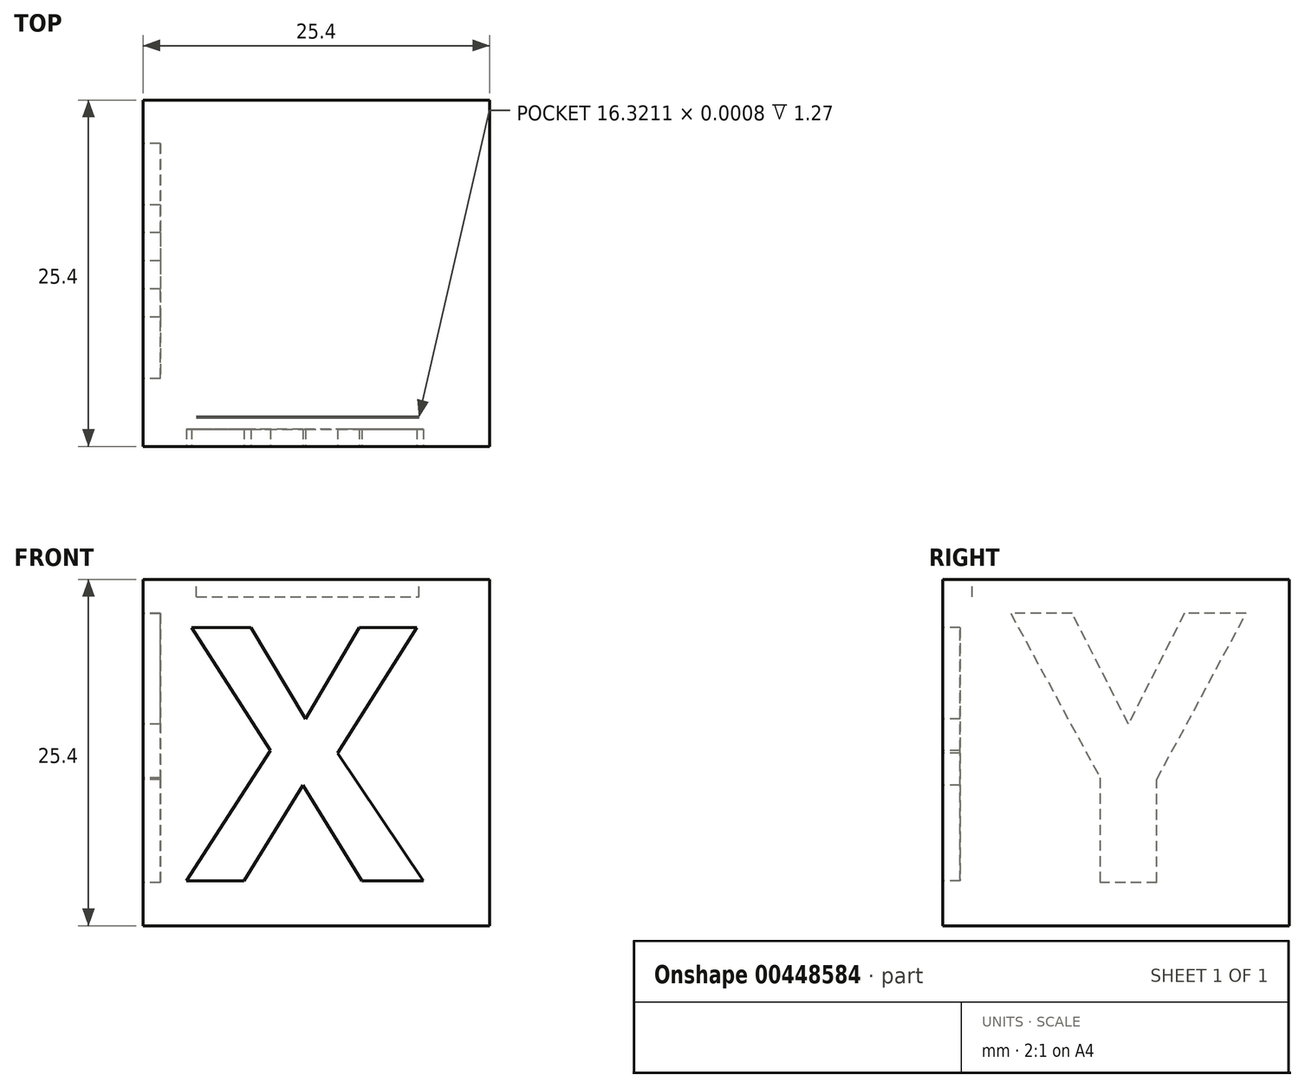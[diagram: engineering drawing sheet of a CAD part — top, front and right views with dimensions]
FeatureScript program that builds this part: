
annotation { "Feature Type Name" : "Feature", "Feature Type Description" : "" }
export const myFeature = defineFeature(function(context is Context, id is Id, definition is map)
    precondition{}
    {
        {
            var Q0;
            Q0=qCreatedBy(makeId("Top.planeOp"),FACE);
            var sketch = newSketch(context, id + "F0", { "sketchPlane" : qUnion([Q0])});
            skLineSegment(sketch, "E0.bottom", {"start": v(12.7, 12.7) * mm, "end": v(-12.7, 12.7) * mm});
            skLineSegment(sketch, "E0.top", {"start": v(12.7, -12.7) * mm, "end": v(-12.7, -12.7) * mm});
            skLineSegment(sketch, "E0.left", {"start": v(12.7, 12.7) * mm, "end": v(12.7, -12.7) * mm});
            skLineSegment(sketch, "E0.right", {"start": v(-12.7, 12.7) * mm, "end": v(-12.7, -12.7) * mm});
            skPoint(sketch, "E0.middle", {"position": v(0, 0) * mm});
            skSolve(sketch);
        }
        {
            var Q0;
            Q0=makeQuery(id+"F0.imprint","IMPRINT",FACE,{"disambiguationData":[TD([[makeQuery(id+"F0.imprint","IMPRINT",EDGE,{"derivedFrom":sQuery(id+"F0.wireOp",EDGE,"E0.bottom")}),1.0]])]});
            extrude(context, id + "F1", {"entities" : qUnion([Q0]), "depth" : 25.4 * mm, "offsetDistance" : 25.4 * mm});
        }
        {
            var Q0;
            Q0=makeQuery(id+"F1.opExtrude","SWEPT_FACE",FACE,{"disambiguationData":[OSD([sQuery(id+"F0.wireOp",EDGE,"E0.top")])]});
            var sketch = newSketch(context, id + "F2", { "sketchPlane" : qUnion([Q0])});
            skLineSegment(sketch, "E1.bottom", {"start": v(9.53, 3.28) * mm, "end": v(-9.53, 3.28) * mm, "construction": true});
            skLineSegment(sketch, "E1.top", {"start": v(9.53, 22.02) * mm, "end": v(-9.53, 22.02) * mm, "construction": true});
            skLineSegment(sketch, "E1.left", {"start": v(9.53, 3.28) * mm, "end": v(9.53, 22.02) * mm, "construction": true});
            skLineSegment(sketch, "E1.right", {"start": v(-9.53, 3.28) * mm, "end": v(-9.53, 22.02) * mm, "construction": true});
            skPoint(sketch, "E1.middle", {"position": v(0, 12.65) * mm});
            skText(sketch, "E2", { "text": "X", "fontName": "OpenSans-Bold.ttf"});
            const initialGuessF2  = {"E2": [-0.00953, 0.00328, 1, 0, 0.01874]};
            skSetInitialGuess(sketch, initialGuessF2);
            skSolve(sketch);
        }
        {
            var Q0;
            Q0=makeQuery(id+"F2.imprint","IMPRINT",FACE,{"disambiguationData":[TD([[makeQuery(id+"F2.imprint","IMPRINT",EDGE,{"derivedFrom":sQuery(id+"F2.wireOp",EDGE,"E2.sketch_text.stroke-0")}),-1.0]])]});
            extrude(context, id + "F3", {"entities" : qUnion([Q0]), "operationType" : NewBodyOperationType.REMOVE, "oppositeDirection" : true, "depth" : 1.27 * mm, "offsetDistance" : 25.4 * mm});
        }
        {
            var Q0;
            Q0=makeQuery(id+"F1.opExtrude","SWEPT_FACE",FACE,{"disambiguationData":[OSD([sQuery(id+"F0.wireOp",EDGE,"E0.right")])]});
            var sketch = newSketch(context, id + "F4", { "sketchPlane" : qUnion([Q0])});
            skLineSegment(sketch, "E3.bottom", {"start": v(-9.53, 3.18) * mm, "end": v(9.53, 3.18) * mm});
            skLineSegment(sketch, "E3.top", {"start": v(-9.53, 23.08) * mm, "end": v(9.52, 23.08) * mm});
            skLineSegment(sketch, "E3.left", {"start": v(-9.53, 3.17) * mm, "end": v(-9.53, 23.08) * mm});
            skLineSegment(sketch, "E3.right", {"start": v(9.53, 3.17) * mm, "end": v(9.52, 23.08) * mm});
            skPoint(sketch, "E3.middle", {"position": v(0, 13.13) * mm});
            skText(sketch, "E4", { "text": "Y", "fontName": "OpenSans-Bold.ttf"});
            const initialGuessF4  = {"E4": [-0.00953, 0.00317, 1, 0, 0.0199]};
            skSetInitialGuess(sketch, initialGuessF4);
            skSolve(sketch);
        }
        {
            var Q0;
            Q0=makeQuery(id+"F4.imprint","IMPRINT",FACE,{"disambiguationData":[TD([[makeQuery(id+"F4.imprint","IMPRINT",EDGE,{"derivedFrom":sQuery(id+"F4.wireOp",EDGE,"E4.sketch_text.stroke-0")}),-1.0]])]});
            extrude(context, id + "F5", {"entities" : qUnion([Q0]), "operationType" : NewBodyOperationType.REMOVE, "oppositeDirection" : true, "depth" : 1.27 * mm, "offsetDistance" : 25.4 * mm});
        }
        {
            var Q0;
            Q0=makeQuery(id+"F1.opExtrude","CAP_FACE",FACE,{"disambiguationData":[OSD([sQuery(id+"F0.wireOp",EDGE,"E0.bottom"),sQuery(id+"F0.wireOp",EDGE,"E0.top"),sQuery(id+"F0.wireOp",EDGE,"E0.left"),sQuery(id+"F0.wireOp",EDGE,"E0.right")])],"isStart":false});
            var sketch = newSketch(context, id + "F6", { "sketchPlane" : qUnion([Q0])});
            skLineSegment(sketch, "E5.bottom", {"start": v(-9.52, -10.55) * mm, "end": v(9.53, -10.55) * mm});
            skLineSegment(sketch, "E5.top", {"start": v(-9.53, 11.57) * mm, "end": v(9.52, 11.57) * mm});
            skLineSegment(sketch, "E5.left", {"start": v(-9.53, -10.55) * mm, "end": v(-9.53, 11.57) * mm});
            skLineSegment(sketch, "E5.right", {"start": v(9.53, -10.55) * mm, "end": v(9.53, 11.57) * mm});
            skPoint(sketch, "E5.middle", {"position": v(0, 0.51) * mm});
            skText(sketch, "E6", { "text": "Z", "fontName": "OpenSans-Bold.ttf"});
            const initialGuessF6  = {"E6": [-0.00952, -0.01055, 1, 0, 0.02212]};
            skSetInitialGuess(sketch, initialGuessF6);
            skSolve(sketch);
        }
        {
            var Q0;
            {var subQ0=sQuery(id+"F6.wireOp",EDGE,"E6.sketch_text.stroke-1");Q0=makeQuery(id+"F6.imprint","IMPRINT",FACE,{"disambiguationData":[TD([[makeQuery(id+"F6.imprint","IMPRINT",EDGE,{"derivedFrom":subQ0}),-1.0]])]});}
            extrude(context, id + "F7", {"entities" : qUnion([Q0]), "operationType" : NewBodyOperationType.REMOVE, "oppositeDirection" : true, "depth" : 1.27 * mm, "offsetDistance" : 25.4 * mm});
        }
    });
